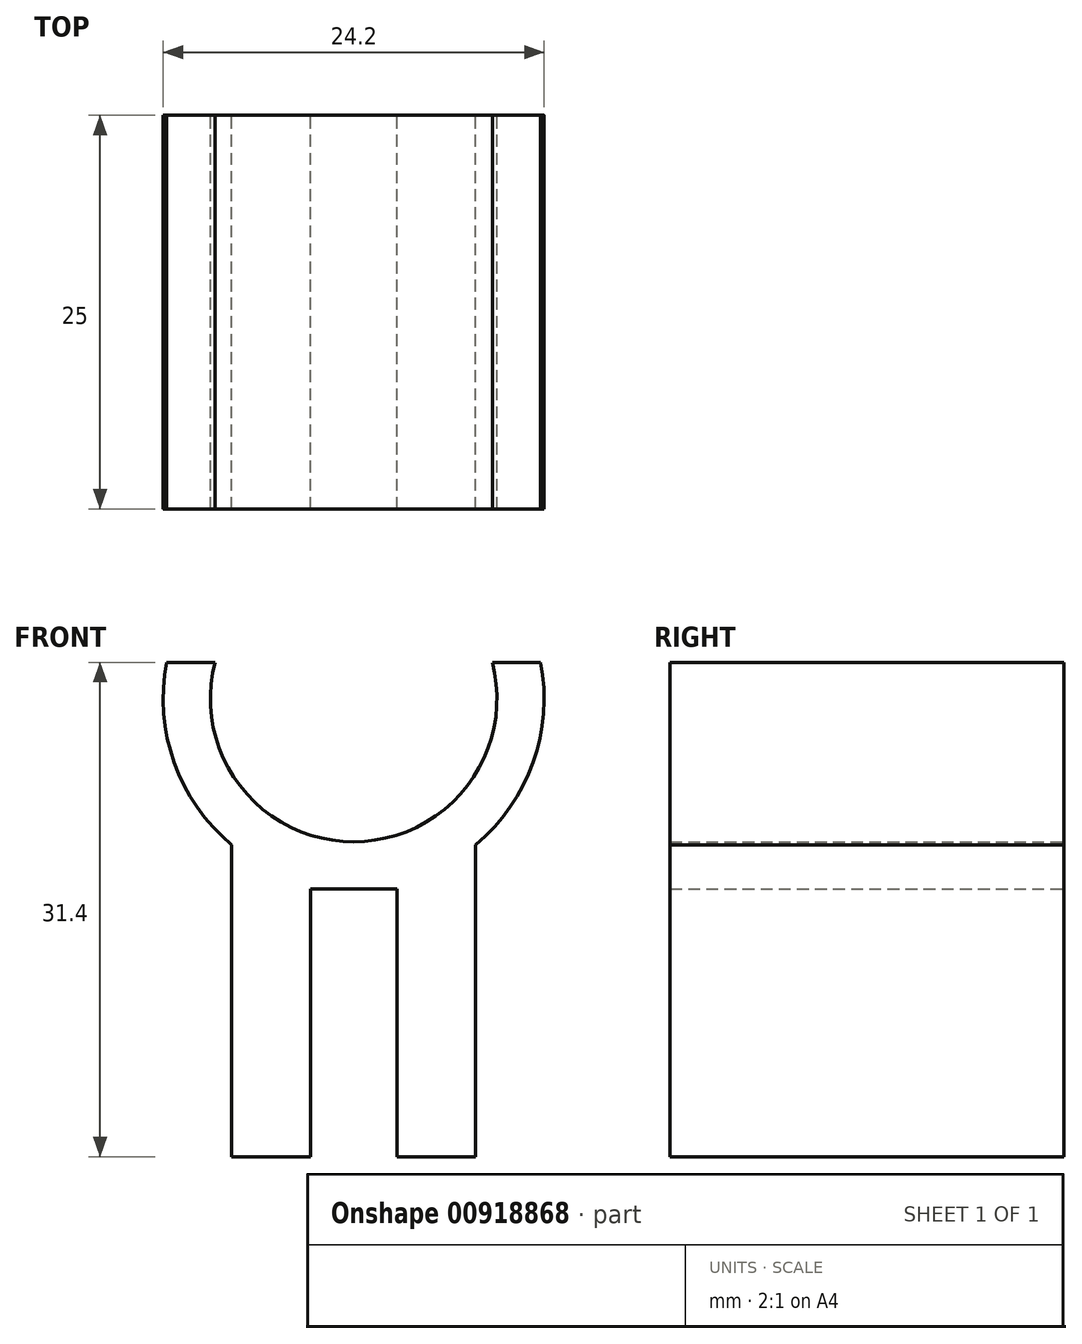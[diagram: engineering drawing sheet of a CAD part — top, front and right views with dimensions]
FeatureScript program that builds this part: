
annotation { "Feature Type Name" : "Feature", "Feature Type Description" : "" }
export const myFeature = defineFeature(function(context is Context, id is Id, definition is map)
    precondition{}
    {
        {
            var Q0;
            Q0=qCreatedBy(makeId("Front.planeOp"),FACE);
            var sketch = newSketch(context, id + "F0", { "sketchPlane" : qUnion([Q0])});
            skLineSegment(sketch, "E0.bottom", {"start": v(-4.17, 7.22) * mm, "end": v(1.33, 7.22) * mm});
            skLineSegment(sketch, "E0.top", {"start": v(-4.17, 10.22) * mm, "end": v(1.33, 10.22) * mm});
            skLineSegment(sketch, "E0.left", {"start": v(-4.17, 7.22) * mm, "end": v(-4.17, 10.22) * mm});
            skLineSegment(sketch, "E0.right", {"start": v(1.33, 7.22) * mm, "end": v(1.33, 10.22) * mm});
            skLineSegment(sketch, "E1.bottom", {"start": v(1.33, 10.22) * mm, "end": v(6.33, 10.22) * mm});
            skLineSegment(sketch, "E1.top", {"start": v(1.33, -9.78) * mm, "end": v(6.33, -9.78) * mm});
            skLineSegment(sketch, "E1.left", {"start": v(1.33, 10.22) * mm, "end": v(1.33, -9.78) * mm});
            skLineSegment(sketch, "E1.right", {"start": v(6.33, 10.22) * mm, "end": v(6.33, -9.78) * mm});
            skLineSegment(sketch, "E2.bottom", {"start": v(-4.17, 10.22) * mm, "end": v(-9.17, 10.22) * mm});
            skLineSegment(sketch, "E2.top", {"start": v(-4.17, -9.78) * mm, "end": v(-9.17, -9.78) * mm});
            skLineSegment(sketch, "E2.left", {"start": v(-4.17, 10.22) * mm, "end": v(-4.17, -9.78) * mm});
            skLineSegment(sketch, "E2.right", {"start": v(-9.17, 10.22) * mm, "end": v(-9.17, -9.78) * mm});
            skCircle(sketch, "E3", {"center": v(-1.42, 19.32) * mm, "radius": 9.1 * mm});
            skPoint(sketch, "E4", {"position": v(-1.42, 10.22) * mm});
            skCircle(sketch, "E5", {"center": v(-1.42, 19.32) * mm, "radius": 12.1 * mm});
            skLineSegment(sketch, "E6", {"start": v(-13.3, 21.62) * mm, "end": v(10.46, 21.62) * mm});
            skSolve(sketch);
        }
        {
            var Q0;
            {var subQ1=sQuery(id+"F0.wireOp",EDGE,"E1.bottom");Q0=makeQuery(id+"F0.imprint","IMPRINT",FACE,{"disambiguationData":[TD([[makeQuery(id+"F0.imprint","IMPRINT",EDGE,{"derivedFrom":subQ1}),1.0]])]});}
            var Q1;
            {var subQ0=sQuery(id+"F0.wireOp",EDGE,"E2.bottom");Q1=makeQuery(id+"F0.imprint","IMPRINT",FACE,{"disambiguationData":[TD([[makeQuery(id+"F0.imprint","IMPRINT",EDGE,{"derivedFrom":subQ0}),1.0]])]});}
            var Q2;
            {var subQ3=sQuery(id+"F0.wireOp",EDGE,"E5");var subQ9=makeQuery(id+"F0.imprint","INTERSECT",VERTEX,{"derivedFrom":[sQuery(id+"F0.wireOp",EDGE,"E0.bottom"),subQ3]});Q2=makeQuery(id+"F0.imprint","IMPRINT",FACE,{"disambiguationData":[TD([[makeQuery(id+"F0.imprint","IMPRINT",EDGE,{"disambiguationData":[TD([[subQ9,1.0]])],"derivedFrom":subQ3}),1.0]])]});}
            var Q3;
            {var subQ0=sQuery(id+"F0.wireOp",EDGE,"E1.bottom");Q3=makeQuery(id+"F0.imprint","IMPRINT",FACE,{"disambiguationData":[TD([[makeQuery(id+"F0.imprint","IMPRINT",EDGE,{"derivedFrom":subQ0}),-1.0]])]});}
            var Q4;
            {var subQ2=sQuery(id+"F0.wireOp",EDGE,"E1.top");Q4=makeQuery(id+"F0.imprint","IMPRINT",FACE,{"disambiguationData":[TD([[makeQuery(id+"F0.imprint","IMPRINT",EDGE,{"derivedFrom":subQ2}),1.0]])]});}
            var Q5;
            {var subQ0=sQuery(id+"F0.wireOp",EDGE,"E1.left");var subQ1=sQuery(id+"F0.wireOp",EDGE,"E0.bottom");var subQ2=makeQuery(id+"F0.imprint","INTERSECT",VERTEX,{"derivedFrom":[subQ1,subQ0]});Q5=makeQuery(id+"F0.imprint","IMPRINT",FACE,{"disambiguationData":[TD([[makeQuery(id+"F0.imprint","IMPRINT",EDGE,{"disambiguationData":[TD([[subQ2,1.0]])],"derivedFrom":subQ1}),1.0]])]});}
            var Q6;
            {var subQ0=sQuery(id+"F0.wireOp",EDGE,"E2.left");var subQ1=sQuery(id+"F0.wireOp",EDGE,"E0.bottom");var subQ2=makeQuery(id+"F0.imprint","INTERSECT",VERTEX,{"derivedFrom":[subQ1,subQ0]});Q6=makeQuery(id+"F0.imprint","IMPRINT",FACE,{"disambiguationData":[TD([[makeQuery(id+"F0.imprint","IMPRINT",EDGE,{"disambiguationData":[TD([[subQ2,-1.0]])],"derivedFrom":subQ1}),1.0]])]});}
            var Q7;
            {var subQ2=sQuery(id+"F0.wireOp",EDGE,"E2.top");Q7=makeQuery(id+"F0.imprint","IMPRINT",FACE,{"disambiguationData":[TD([[makeQuery(id+"F0.imprint","IMPRINT",EDGE,{"derivedFrom":subQ2}),-1.0]])]});}
            var Q8;
            {var subQ6=sQuery(id+"F0.wireOp",EDGE,"E2.bottom");Q8=makeQuery(id+"F0.imprint","IMPRINT",FACE,{"disambiguationData":[TD([[makeQuery(id+"F0.imprint","IMPRINT",EDGE,{"derivedFrom":subQ6}),-1.0]])]});}
            extrude(context, id + "F1", {"entities" : qUnion([Q0, Q1, Q2, Q3, Q4, Q5, Q6, Q7, Q8]), "depth" : 25 * mm, "offsetDistance" : 25 * mm});
        }
    });
